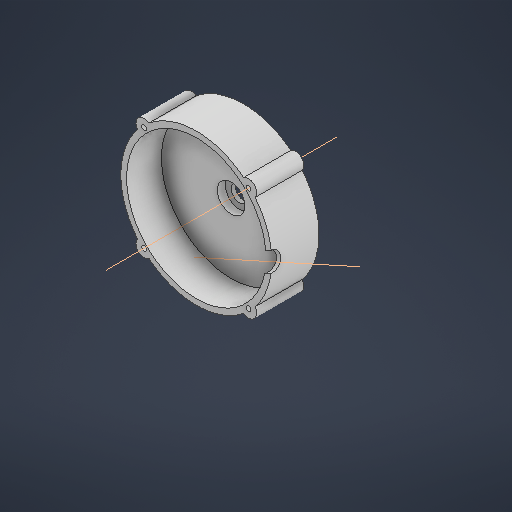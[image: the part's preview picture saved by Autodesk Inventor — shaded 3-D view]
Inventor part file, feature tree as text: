
AUTODESK INVENTOR PART (.ipt)
format: ipt  version: 2025.3 (Build 293356030, 356C)  size: 291,328 bytes
history: native  units: mm
features: sketch x6, extrude x5, other x3, plane x2
ambient origin geometry x8: Origin, YZ Plane, XZ Plane, XY Plane, X Axis, Y Axis, Z Axis, Center Point
bodies: Solid1 (feature_tree)
feature tree (16):
  sketch  "Sketch1"  dims[d0=10.0mm d1=16.9mm]
  extrude  "Extrusion1"  Depth=10.0mm
  extrude  "Extrusion3"  Depth=90.0mm
  extrude  "Extrusion4"  Depth=5.0mm
  sketch  "Sketch2"  dims[d4=2.9mm d5=5.0mm]
  plane  "Work Plane1"
  sketch  "Sketch3"  dims[d6=40.0mm d8=360.0deg d10=68.0mm]
  plane  "Work Plane2"
  extrude  "Extrusion5"  Depth=68.0mm
  other  "Work Axis1"
  other  "Work Axis2"
  other  "Work Axis3"
  extrude  "Extrusion6"  Depth=3.75mm TaperAngle=0.0deg
  sketch  "Sketch Circular Pattern1"  dims[d2=85.0mm d3=90.0mm]
  sketch  "Sketch4"  dims[d12=7.5mm d13=0.0mm d16=3.75mm d17=0.0mm]
  sketch  "Sketch5"  dims[d18=25.0mm d19=0.0mm d20=-13.089969mm d21=-5.235988mm d22=10.65mm d23=25.0mm d24=0.0mm d25=92.0mm d26=2.5mm d27=0.0mm d14=0.5mm d15=0.872665mm]
